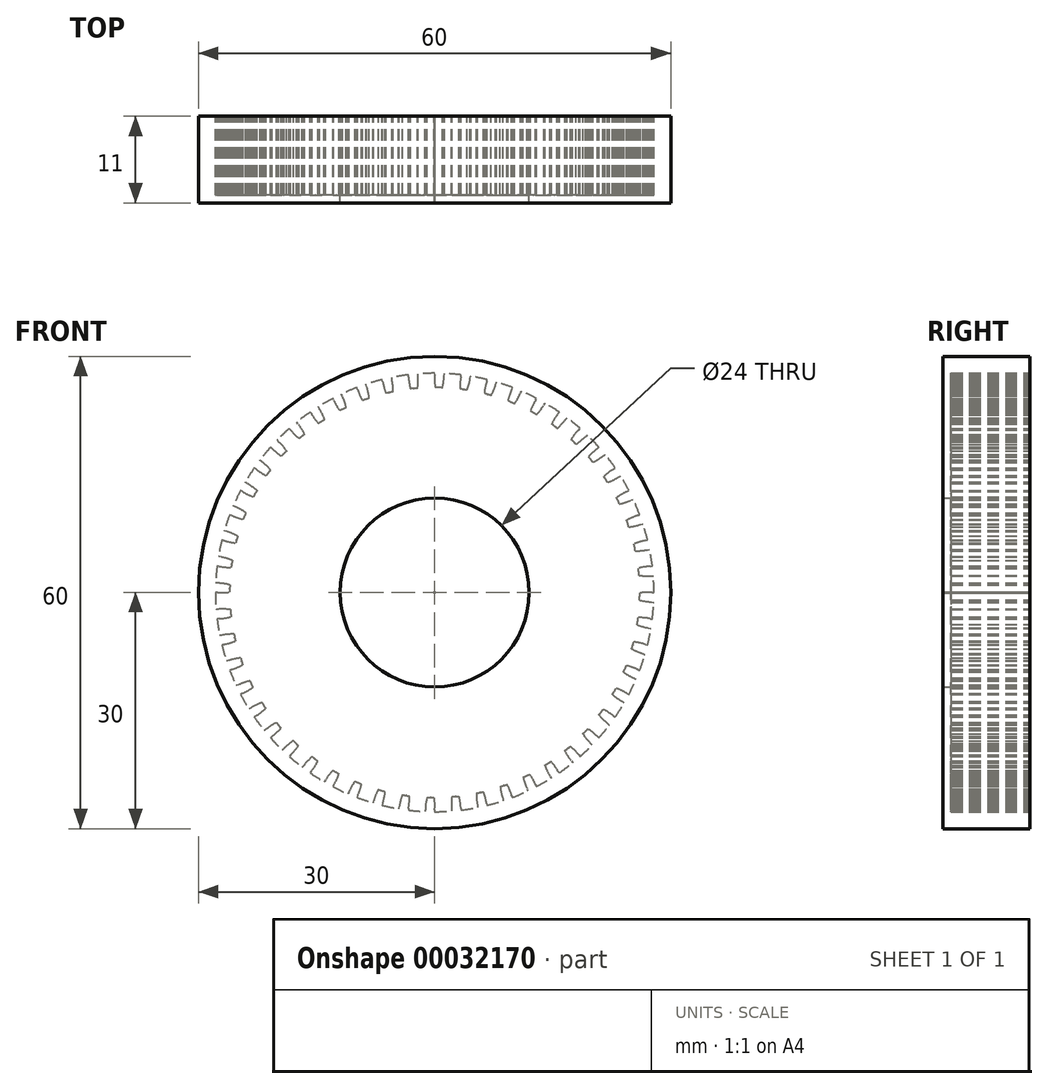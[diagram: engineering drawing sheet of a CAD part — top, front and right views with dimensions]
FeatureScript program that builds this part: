
annotation { "Feature Type Name" : "Feature", "Feature Type Description" : "" }
export const myFeature = defineFeature(function(context is Context, id is Id, definition is map)
    precondition{}
    {
        {
            var Q0;
            Q0=qCreatedBy(makeId("Front.planeOp"),FACE);
            var sketch = newSketch(context, id + "F0", { "sketchPlane" : qUnion([Q0])});
            skArc(sketch, "E0", {"start": v(-0.76, 9.47) * mm, "mid": v(-0.88, 9.46) * mm, "end": v(-1, 9.45) * mm});
            skArc(sketch, "E1", {"start": v(-1.33, 7.13) * mm, "mid": v(-1.98, 6.97) * mm, "end": v(-2.62, 6.76) * mm});
            skLineSegment(sketch, "E2", {"start": v(0, 7.25) * mm, "end": v(0, 8.5) * mm});
            skArc(sketch, "E3", {"start": v(0, 8.5) * mm, "mid": v(-0.3, 9.04) * mm, "end": v(-0.76, 9.47) * mm});
            skArc(sketch, "E4.0.MirrorCS", {"start": v(-1.56, 8.36) * mm, "mid": v(-1.36, 8.94) * mm, "end": v(-1, 9.45) * mm});
            skLineSegment(sketch, "E5.0.MirrorCS", {"start": v(-1.33, 7.13) * mm, "end": v(-1.56, 8.36) * mm});
            skLineSegment(sketch, "E6.1.0", {"start": v(-2.62, 6.76) * mm, "end": v(-3.07, 7.93) * mm});
            skArc(sketch, "E6.1.1", {"start": v(-4.47, 7.23) * mm, "mid": v(-4.5, 7.85) * mm, "end": v(-4.34, 8.45) * mm});
            skArc(sketch, "E6.1.2", {"start": v(-3.07, 7.93) * mm, "mid": v(-3.55, 8.32) * mm, "end": v(-4.13, 8.56) * mm});
            skLineSegment(sketch, "E6.1.3", {"start": v(-3.82, 6.16) * mm, "end": v(-4.47, 7.23) * mm});
            skArc(sketch, "E6.1.4", {"start": v(-4.13, 8.56) * mm, "mid": v(-4.23, 8.5) * mm, "end": v(-4.34, 8.45) * mm});
            skLineSegment(sketch, "E6.2.0", {"start": v(-4.88, 5.36) * mm, "end": v(-5.73, 6.28) * mm});
            skArc(sketch, "E6.2.1", {"start": v(-6.78, 5.12) * mm, "mid": v(-7.03, 5.7) * mm, "end": v(-7.1, 6.31) * mm});
            skArc(sketch, "E6.2.2", {"start": v(-5.73, 6.28) * mm, "mid": v(-6.32, 6.48) * mm, "end": v(-6.94, 6.49) * mm});
            skLineSegment(sketch, "E6.2.3", {"start": v(-5.78, 4.37) * mm, "end": v(-6.78, 5.12) * mm});
            skArc(sketch, "E6.2.4", {"start": v(-6.94, 6.49) * mm, "mid": v(-7.02, 6.4) * mm, "end": v(-7.1, 6.31) * mm});
            skLineSegment(sketch, "E6.3.0", {"start": v(-6.49, 3.23) * mm, "end": v(-7.6, 3.79) * mm});
            skArc(sketch, "E6.3.1", {"start": v(-8.18, 2.33) * mm, "mid": v(-8.61, 2.77) * mm, "end": v(-8.9, 3.32) * mm});
            skArc(sketch, "E6.3.2", {"start": v(-7.6, 3.79) * mm, "mid": v(-8.23, 3.76) * mm, "end": v(-8.81, 3.54) * mm});
            skLineSegment(sketch, "E6.3.3", {"start": v(-6.97, 1.99) * mm, "end": v(-8.18, 2.33) * mm});
            skArc(sketch, "E6.3.4", {"start": v(-8.81, 3.54) * mm, "mid": v(-8.86, 3.43) * mm, "end": v(-8.9, 3.32) * mm});
            skLineSegment(sketch, "E6.4.0", {"start": v(-7.22, 0.67) * mm, "end": v(-8.46, 0.78) * mm});
            skArc(sketch, "E6.4.1", {"start": v(-8.46, -0.78) * mm, "mid": v(-9.03, -0.53) * mm, "end": v(-9.5, -0.12) * mm});
            skArc(sketch, "E6.4.2", {"start": v(-8.46, 0.78) * mm, "mid": v(-9.03, 0.53) * mm, "end": v(-9.5, 0.12) * mm});
            skLineSegment(sketch, "E6.4.3", {"start": v(-7.22, -0.67) * mm, "end": v(-8.46, -0.78) * mm});
            skArc(sketch, "E6.4.4", {"start": v(-9.5, 0.12) * mm, "mid": v(-9.5, 0) * mm, "end": v(-9.5, -0.12) * mm});
            skLineSegment(sketch, "E6.5.0", {"start": v(-6.97, -1.98) * mm, "end": v(-8.18, -2.33) * mm});
            skArc(sketch, "E6.5.1", {"start": v(-7.6, -3.79) * mm, "mid": v(-8.23, -3.75) * mm, "end": v(-8.81, -3.54) * mm});
            skArc(sketch, "E6.5.2", {"start": v(-8.18, -2.33) * mm, "mid": v(-8.61, -2.77) * mm, "end": v(-8.9, -3.32) * mm});
            skLineSegment(sketch, "E6.5.3", {"start": v(-6.5, -3.23) * mm, "end": v(-7.6, -3.79) * mm});
            skArc(sketch, "E6.5.4", {"start": v(-8.9, -3.32) * mm, "mid": v(-8.86, -3.43) * mm, "end": v(-8.81, -3.54) * mm});
            skLineSegment(sketch, "E6.6.0", {"start": v(-5.79, -4.37) * mm, "end": v(-6.78, -5.12) * mm});
            skArc(sketch, "E6.6.1", {"start": v(-5.73, -6.28) * mm, "mid": v(-6.32, -6.47) * mm, "end": v(-6.94, -6.49) * mm});
            skArc(sketch, "E6.6.2", {"start": v(-6.78, -5.12) * mm, "mid": v(-7.03, -5.7) * mm, "end": v(-7.1, -6.3) * mm});
            skLineSegment(sketch, "E6.6.3", {"start": v(-4.89, -5.36) * mm, "end": v(-5.73, -6.28) * mm});
            skArc(sketch, "E6.6.4", {"start": v(-7.1, -6.3) * mm, "mid": v(-7.02, -6.4) * mm, "end": v(-6.94, -6.49) * mm});
            skLineSegment(sketch, "E6.7.0", {"start": v(-3.82, -6.16) * mm, "end": v(-4.47, -7.23) * mm});
            skArc(sketch, "E6.7.1", {"start": v(-3.07, -7.93) * mm, "mid": v(-3.55, -8.32) * mm, "end": v(-4.13, -8.56) * mm});
            skArc(sketch, "E6.7.2", {"start": v(-4.47, -7.23) * mm, "mid": v(-4.5, -7.85) * mm, "end": v(-4.34, -8.45) * mm});
            skLineSegment(sketch, "E6.7.3", {"start": v(-2.62, -6.76) * mm, "end": v(-3.07, -7.93) * mm});
            skArc(sketch, "E6.7.4", {"start": v(-4.34, -8.45) * mm, "mid": v(-4.24, -8.5) * mm, "end": v(-4.13, -8.56) * mm});
            skLineSegment(sketch, "E6.8.0", {"start": v(-1.33, -7.13) * mm, "end": v(-1.56, -8.36) * mm});
            skArc(sketch, "E6.8.1", {"start": v(0, -8.5) * mm, "mid": v(-0.3, -9.04) * mm, "end": v(-0.76, -9.47) * mm});
            skArc(sketch, "E6.8.2", {"start": v(-1.56, -8.36) * mm, "mid": v(-1.36, -8.94) * mm, "end": v(-1, -9.45) * mm});
            skLineSegment(sketch, "E6.8.3", {"start": v(0, -7.25) * mm, "end": v(0, -8.5) * mm});
            skArc(sketch, "E6.8.4", {"start": v(-1, -9.45) * mm, "mid": v(-0.88, -9.46) * mm, "end": v(-0.76, -9.47) * mm});
            skLineSegment(sketch, "E6.9.0", {"start": v(1.33, -7.13) * mm, "end": v(1.56, -8.36) * mm});
            skArc(sketch, "E6.9.1", {"start": v(3.07, -7.93) * mm, "mid": v(2.98, -8.54) * mm, "end": v(2.72, -9.1) * mm});
            skArc(sketch, "E6.9.2", {"start": v(1.56, -8.36) * mm, "mid": v(1.96, -8.83) * mm, "end": v(2.48, -9.17) * mm});
            skLineSegment(sketch, "E6.9.3", {"start": v(2.62, -6.76) * mm, "end": v(3.07, -7.93) * mm});
            skArc(sketch, "E6.9.4", {"start": v(2.48, -9.17) * mm, "mid": v(2.6, -9.14) * mm, "end": v(2.72, -9.1) * mm});
            skLineSegment(sketch, "E6.10.0", {"start": v(3.82, -6.16) * mm, "end": v(4.47, -7.23) * mm});
            skArc(sketch, "E6.10.1", {"start": v(5.73, -6.28) * mm, "mid": v(5.86, -6.89) * mm, "end": v(5.82, -7.5) * mm});
            skArc(sketch, "E6.10.2", {"start": v(4.47, -7.23) * mm, "mid": v(5.02, -7.53) * mm, "end": v(5.63, -7.65) * mm});
            skLineSegment(sketch, "E6.10.3", {"start": v(4.88, -5.36) * mm, "end": v(5.73, -6.28) * mm});
            skArc(sketch, "E6.10.4", {"start": v(5.63, -7.65) * mm, "mid": v(5.72, -7.58) * mm, "end": v(5.82, -7.5) * mm});
            skLineSegment(sketch, "E6.11.0", {"start": v(5.79, -4.37) * mm, "end": v(6.78, -5.12) * mm});
            skArc(sketch, "E6.11.1", {"start": v(7.6, -3.79) * mm, "mid": v(7.96, -4.3) * mm, "end": v(8.14, -4.9) * mm});
            skArc(sketch, "E6.11.2", {"start": v(6.78, -5.12) * mm, "mid": v(7.4, -5.2) * mm, "end": v(8.01, -5.1) * mm});
            skLineSegment(sketch, "E6.11.3", {"start": v(6.49, -3.23) * mm, "end": v(7.6, -3.79) * mm});
            skArc(sketch, "E6.11.4", {"start": v(8.01, -5.1) * mm, "mid": v(8.08, -5) * mm, "end": v(8.14, -4.9) * mm});
            skLineSegment(sketch, "E6.12.0", {"start": v(6.97, -1.98) * mm, "end": v(8.18, -2.33) * mm});
            skArc(sketch, "E6.12.1", {"start": v(8.46, -0.79) * mm, "mid": v(8.97, -1.14) * mm, "end": v(9.36, -1.63) * mm});
            skArc(sketch, "E6.12.2", {"start": v(8.18, -2.33) * mm, "mid": v(8.78, -2.18) * mm, "end": v(9.32, -1.86) * mm});
            skLineSegment(sketch, "E6.12.3", {"start": v(7.22, -0.67) * mm, "end": v(8.46, -0.79) * mm});
            skArc(sketch, "E6.12.4", {"start": v(9.32, -1.86) * mm, "mid": v(9.34, -1.75) * mm, "end": v(9.36, -1.63) * mm});
            skLineSegment(sketch, "E6.13.0", {"start": v(7.22, 0.67) * mm, "end": v(8.46, 0.78) * mm});
            skArc(sketch, "E6.13.1", {"start": v(8.18, 2.32) * mm, "mid": v(8.78, 2.18) * mm, "end": v(9.32, 1.86) * mm});
            skArc(sketch, "E6.13.2", {"start": v(8.46, 0.78) * mm, "mid": v(8.97, 1.14) * mm, "end": v(9.36, 1.63) * mm});
            skLineSegment(sketch, "E6.13.3", {"start": v(6.97, 1.98) * mm, "end": v(8.18, 2.32) * mm});
            skArc(sketch, "E6.13.4", {"start": v(9.36, 1.63) * mm, "mid": v(9.34, 1.74) * mm, "end": v(9.32, 1.86) * mm});
            skLineSegment(sketch, "E6.14.0", {"start": v(6.49, 3.23) * mm, "end": v(7.6, 3.79) * mm});
            skArc(sketch, "E6.14.1", {"start": v(6.78, 5.12) * mm, "mid": v(7.4, 5.2) * mm, "end": v(8.01, 5.1) * mm});
            skArc(sketch, "E6.14.2", {"start": v(7.6, 3.79) * mm, "mid": v(7.96, 4.3) * mm, "end": v(8.14, 4.9) * mm});
            skLineSegment(sketch, "E6.14.3", {"start": v(5.79, 4.37) * mm, "end": v(6.78, 5.12) * mm});
            skArc(sketch, "E6.14.4", {"start": v(8.14, 4.9) * mm, "mid": v(8.08, 5) * mm, "end": v(8.01, 5.1) * mm});
            skLineSegment(sketch, "E6.15.0", {"start": v(4.88, 5.36) * mm, "end": v(5.73, 6.28) * mm});
            skArc(sketch, "E6.15.1", {"start": v(4.48, 7.23) * mm, "mid": v(5.02, 7.52) * mm, "end": v(5.63, 7.65) * mm});
            skArc(sketch, "E6.15.2", {"start": v(5.73, 6.28) * mm, "mid": v(5.86, 6.89) * mm, "end": v(5.82, 7.5) * mm});
            skLineSegment(sketch, "E6.15.3", {"start": v(3.82, 6.16) * mm, "end": v(4.48, 7.23) * mm});
            skArc(sketch, "E6.15.4", {"start": v(5.82, 7.5) * mm, "mid": v(5.73, 7.58) * mm, "end": v(5.63, 7.65) * mm});
            skLineSegment(sketch, "E6.16.0", {"start": v(2.62, 6.76) * mm, "end": v(3.07, 7.93) * mm});
            skArc(sketch, "E6.16.1", {"start": v(1.56, 8.36) * mm, "mid": v(1.96, 8.83) * mm, "end": v(2.48, 9.17) * mm});
            skArc(sketch, "E6.16.2", {"start": v(3.07, 7.93) * mm, "mid": v(2.98, 8.54) * mm, "end": v(2.72, 9.1) * mm});
            skLineSegment(sketch, "E6.16.3", {"start": v(1.33, 7.13) * mm, "end": v(1.56, 8.36) * mm});
            skArc(sketch, "E6.16.4", {"start": v(2.72, 9.1) * mm, "mid": v(2.6, 9.14) * mm, "end": v(2.48, 9.17) * mm});
            skArc(sketch, "E7.trimOffspring", {"start": v(1.33, 7.13) * mm, "mid": v(0.67, 7.22) * mm, "end": v(0, 7.25) * mm});
            skArc(sketch, "E8.trimOffspring", {"start": v(3.82, 6.16) * mm, "mid": v(3.23, 6.49) * mm, "end": v(2.62, 6.76) * mm});
            skArc(sketch, "E9.trimOffspring", {"start": v(5.79, 4.37) * mm, "mid": v(5.36, 4.88) * mm, "end": v(4.88, 5.36) * mm});
            skArc(sketch, "E10.trimOffspring", {"start": v(6.97, 1.98) * mm, "mid": v(6.76, 2.62) * mm, "end": v(6.49, 3.23) * mm});
            skArc(sketch, "E11.trimOffspring", {"start": v(7.22, -0.67) * mm, "mid": v(7.25, 0) * mm, "end": v(7.22, 0.67) * mm});
            skArc(sketch, "E12.trimOffspring", {"start": v(6.49, -3.23) * mm, "mid": v(6.76, -2.62) * mm, "end": v(6.97, -1.98) * mm});
            skArc(sketch, "E13.trimOffspring", {"start": v(4.88, -5.36) * mm, "mid": v(5.36, -4.88) * mm, "end": v(5.79, -4.37) * mm});
            skArc(sketch, "E14.trimOffspring", {"start": v(2.62, -6.76) * mm, "mid": v(3.23, -6.5) * mm, "end": v(3.82, -6.16) * mm});
            skArc(sketch, "E15.trimOffspring", {"start": v(0, -7.25) * mm, "mid": v(0.67, -7.22) * mm, "end": v(1.33, -7.13) * mm});
            skArc(sketch, "E16.trimOffspring", {"start": v(-2.62, -6.76) * mm, "mid": v(-1.98, -6.97) * mm, "end": v(-1.33, -7.13) * mm});
            skArc(sketch, "E17.trimOffspring", {"start": v(-4.89, -5.36) * mm, "mid": v(-4.37, -5.79) * mm, "end": v(-3.82, -6.16) * mm});
            skArc(sketch, "E18.trimOffspring", {"start": v(-6.5, -3.23) * mm, "mid": v(-6.16, -3.82) * mm, "end": v(-5.79, -4.37) * mm});
            skArc(sketch, "E19.trimOffspring", {"start": v(-7.22, -0.67) * mm, "mid": v(-7.13, -1.33) * mm, "end": v(-6.97, -1.98) * mm});
            skArc(sketch, "E20.trimOffspring", {"start": v(-6.97, 1.99) * mm, "mid": v(-7.13, 1.33) * mm, "end": v(-7.22, 0.67) * mm});
            skArc(sketch, "E21.trimOffspring", {"start": v(-5.78, 4.37) * mm, "mid": v(-6.16, 3.82) * mm, "end": v(-6.49, 3.23) * mm});
            skArc(sketch, "E22.trimOffspring", {"start": v(-3.82, 6.16) * mm, "mid": v(-4.37, 5.79) * mm, "end": v(-4.88, 5.36) * mm});
            skCircle(sketch, "E23", {"center": v(0, 0) * mm, "radius": 4 * mm});
            skLineSegment(sketch, "E24", {"start": v(-0.42, 17.6) * mm, "end": v(1.16, 17.6) * mm, "construction": true});
            skLineSegment(sketch, "E25", {"start": v(0, 18.2) * mm, "end": v(0, 16.94) * mm, "construction": true});
            skArc(sketch, "E26", {"start": v(-3.08, 26.06) * mm, "mid": v(-1.05, 8.66) * mm, "end": v(4.95, 25.12) * mm});
            skArc(sketch, "E27", {"start": v(-0.73, 27.57) * mm, "mid": v(-0.8, 27.57) * mm, "end": v(-0.87, 27.56) * mm});
            skArc(sketch, "E28", {"start": v(-0.79, 26.59) * mm, "mid": v(0.12, -26.6) * mm, "end": v(0.54, 26.6) * mm});
            skCircle(sketch, "E29", {"center": v(0, 17.6) * mm, "radius": 7.75 * mm});
            skCircle(sketch, "E30", {"center": v(0, 0) * mm, "radius": 27.85 * mm});
            skCircle(sketch, "E31", {"center": v(0, 0) * mm, "radius": 25.6 * mm});
            skArc(sketch, "E32", {"start": v(-1.47, 25.93) * mm, "mid": v(-2.4, 25.7) * mm, "end": v(-3.3, 25.39) * mm});
            skLineSegment(sketch, "E33", {"start": v(0, 17.6) * mm, "end": v(0, 26.6) * mm, "construction": true});
            skLineSegment(sketch, "E34", {"start": v(0, 17.6) * mm, "end": v(-0.98, 28.75) * mm, "construction": true});
            skCircle(sketch, "E35", {"center": v(0, 17.6) * mm, "radius": 8 * mm, "construction": true});
            skLineSegment(sketch, "E36", {"start": v(0, 26.6) * mm, "end": v(0, 26.06) * mm});
            skLineSegment(sketch, "E37.trimOffspring", {"start": v(0, 25.6) * mm, "end": v(0, 25.6) * mm});
            skArc(sketch, "E38.trimOffspring", {"start": v(-5.33, 26.06) * mm, "mid": v(2.49, 7.91) * mm, "end": v(0.6, 27.58) * mm});
            skArc(sketch, "E39.0.MirrorCS", {"start": v(-1.02, 27.55) * mm, "mid": v(-0.94, 27.56) * mm, "end": v(-0.87, 27.56) * mm});
            skArc(sketch, "E40.0.MirrorCS", {"start": v(-1.56, 26.46) * mm, "mid": v(-1.36, 27.04) * mm, "end": v(-1.02, 27.55) * mm});
            skLineSegment(sketch, "E41.0.MirrorCS", {"start": v(-1.56, 26.46) * mm, "end": v(-1.47, 25.93) * mm});
            skLineSegment(sketch, "E42", {"start": v(0, 17.6) * mm, "end": v(-4, 28.58) * mm, "construction": true});
            skArc(sketch, "E43.trimOffspring", {"start": v(-1.18, 9.23) * mm, "mid": v(8.41, 16.75) * mm, "end": v(0.51, 26.04) * mm});
            skLineSegment(sketch, "E44", {"start": v(0, 17.6) * mm, "end": v(0.98, 17.69) * mm, "construction": true});
            skArc(sketch, "E45.0.MirrorCS", {"start": v(0, 8.6) * mm, "mid": v(0.3, 8.06) * mm, "end": v(0.73, 7.63) * mm});
            skLineSegment(sketch, "E46.0.MirrorCS", {"start": v(0, 8.6) * mm, "end": v(0, 9.14) * mm});
            skArc(sketch, "E47.0.MirrorCS", {"start": v(1.56, 8.74) * mm, "mid": v(1.36, 8.16) * mm, "end": v(1.02, 7.65) * mm});
            skLineSegment(sketch, "E48.0.MirrorCS", {"start": v(1.56, 8.74) * mm, "end": v(1.47, 9.27) * mm});
            skArc(sketch, "E49.0.MirrorCS", {"start": v(1.02, 7.65) * mm, "mid": v(0.94, 7.64) * mm, "end": v(0.87, 7.64) * mm});
            skArc(sketch, "E49.1.MirrorCS", {"start": v(0.73, 7.63) * mm, "mid": v(0.8, 7.63) * mm, "end": v(0.87, 7.64) * mm});
            skLineSegment(sketch, "E50", {"start": v(0, 0) * mm, "end": v(0, -29.5) * mm, "construction": true});
            skLineSegment(sketch, "E51", {"start": v(0, 0) * mm, "end": v(1.8, -29.89) * mm, "construction": true});
            skLineSegment(sketch, "E52", {"start": v(0, 0) * mm, "end": v(0.96, -31.81) * mm, "construction": true});
            skLineSegment(sketch, "E53", {"start": v(0, 17.6) * mm, "end": v(1.5, 29.97) * mm, "construction": true});
            skLineSegment(sketch, "E54", {"start": v(0, 17.6) * mm, "end": v(0.42, 31.47) * mm, "construction": true});
            skCircle(sketch, "E55", {"center": v(0, 0) * mm, "radius": 25 * mm, "construction": true});
            skArc(sketch, "E56.trimOffspring", {"start": v(0, 27.6) * mm, "mid": v(-0.01, 26.83) * mm, "end": v(0.06, 26.05) * mm});
            skArc(sketch, "E57.trimOffspring", {"start": v(0.26, 26.05) * mm, "mid": v(0.16, 26.05) * mm, "end": v(0.06, 26.05) * mm});
            skLineSegment(sketch, "E58.0.MirrorCS", {"start": v(0.54, 26.58) * mm, "end": v(0.66, 28.55) * mm, "construction": true});
            skArc(sketch, "E59.0.MirrorCS", {"start": v(0.26, 26.05) * mm, "mid": v(0.35, 26.05) * mm, "end": v(0.45, 26.04) * mm});
            skCircle(sketch, "E60", {"center": v(0, 0) * mm, "radius": 30 * mm});
            skCircle(sketch, "E61", {"center": v(0, 0) * mm, "radius": 0.05 * mm});
            skArc(sketch, "E62.trimOffspring", {"start": v(0.54, 26.6) * mm, "mid": v(0.54, 26.59) * mm, "end": v(0.54, 26.58) * mm});
            skArc(sketch, "E63.0.MirrorCS", {"start": v(1.2, 27.53) * mm, "mid": v(1.12, 26.76) * mm, "end": v(0.96, 26) * mm});
            skArc(sketch, "E64.0.MirrorCS", {"start": v(0.76, 26.02) * mm, "mid": v(0.86, 26.01) * mm, "end": v(0.96, 26) * mm});
            skArc(sketch, "E65.0.MirrorCS", {"start": v(0.76, 26.02) * mm, "mid": v(0.67, 26.03) * mm, "end": v(0.57, 26.04) * mm});
            skLineSegment(sketch, "E66.0.MirrorCS", {"start": v(1.2, 27.53) * mm, "end": v(1.23, 27.78) * mm});
            skLineSegment(sketch, "E67", {"start": v(0.45, 26.04) * mm, "end": v(0.51, 26.04) * mm});
            skPoint(sketch, "E68.end.orphan", {"position": v(0, 27.85) * mm});
            skLineSegment(sketch, "E69", {"start": v(0, 27.6) * mm, "end": v(0, 27.85) * mm});
            skLineSegment(sketch, "E70", {"start": v(1.23, 27.78) * mm, "end": v(1.24, 27.82) * mm});
            skSolve(sketch);
        }
        {
            var Q0;
            Q0=makeQuery(id+"F0.imprint","IMPRINT",FACE,{"disambiguationData":[TD([[makeQuery(id+"F0.imprint","IMPRINT",EDGE,{"derivedFrom":sQuery(id+"F0.wireOp",EDGE,"E60")}),1.0]])]});
            var Q1;
            {var subQ7=sQuery(id+"F0.wireOp",EDGE,"E57.trimOffspring");Q1=makeQuery(id+"F0.imprint","IMPRINT",FACE,{"disambiguationData":[TD([[makeQuery(id+"F0.imprint","IMPRINT",EDGE,{"derivedFrom":subQ7}),-1.0]])]});}
            var Q2;
            Q2=makeQuery(id+"F0.imprint","IMPRINT",FACE,{"disambiguationData":[TD([[makeQuery(id+"F0.imprint","IMPRINT",EDGE,{"derivedFrom":sQuery(id+"F0.wireOp",EDGE,"E61")}),1.0]])]});
            extrude(context, id + "F1", {"entities" : qUnion([Q0, Q1, Q2]), "depth" : 10 * mm});
        }
        {
            var Q0;
            Q0=makeQuery(id+"F1.opExtrude","SWEPT_BODY",BODY,{"disambiguationData":[OSD([sQuery(id+"F0.wireOp",EDGE,"E30"),sQuery(id+"F0.wireOp",EDGE,"E43.trimOffspring"),sQuery(id+"F0.wireOp",EDGE,"E56.trimOffspring"),sQuery(id+"F0.wireOp",EDGE,"E57.trimOffspring"),sQuery(id+"F0.wireOp",EDGE,"E59.0.MirrorCS"),sQuery(id+"F0.wireOp",EDGE,"E60"),sQuery(id+"F0.wireOp",EDGE,"E63.0.MirrorCS"),sQuery(id+"F0.wireOp",EDGE,"E64.0.MirrorCS"),sQuery(id+"F0.wireOp",EDGE,"E65.0.MirrorCS"),sQuery(id+"F0.wireOp",EDGE,"E66.0.MirrorCS"),sQuery(id+"F0.wireOp",EDGE,"E67"),sQuery(id+"F0.wireOp",EDGE,"E69"),sQuery(id+"F0.wireOp",EDGE,"E70")])]});
            var Q1;
            Q1=makeQuery(id+"F1.opExtrude","SWEPT_FACE",FACE,{"disambiguationData":[OSD([sQuery(id+"F0.wireOp",EDGE,"E61")])]});
            circularPattern(context, id + "F2", {"entities" : qUnion([Q0]), "axis" : qUnion([Q1]), "angle" : 6.92 * degree, "instanceCount" : round(52)});
        }
        {
            var Q0;
            Q0=makeQuery(id+"F2.opPattern","COPY",FACE,{"derivedFrom":makeQuery(id+"F1.opExtrude","CAP_FACE",FACE,{"disambiguationData":[OSD([sQuery(id+"F0.wireOp",EDGE,"E30"),sQuery(id+"F0.wireOp",EDGE,"E43.trimOffspring"),sQuery(id+"F0.wireOp",EDGE,"E56.trimOffspring"),sQuery(id+"F0.wireOp",EDGE,"E57.trimOffspring"),sQuery(id+"F0.wireOp",EDGE,"E59.0.MirrorCS"),sQuery(id+"F0.wireOp",EDGE,"E60"),sQuery(id+"F0.wireOp",EDGE,"E63.0.MirrorCS"),sQuery(id+"F0.wireOp",EDGE,"E64.0.MirrorCS"),sQuery(id+"F0.wireOp",EDGE,"E65.0.MirrorCS"),sQuery(id+"F0.wireOp",EDGE,"E66.0.MirrorCS"),sQuery(id+"F0.wireOp",EDGE,"E67"),sQuery(id+"F0.wireOp",EDGE,"E69"),sQuery(id+"F0.wireOp",EDGE,"E70")])],"isStart":false}),"instanceName":"44"});
            var sketch = newSketch(context, id + "F3", { "sketchPlane" : qUnion([Q0])});
            skCircle(sketch, "E71.0", {"center": v(0, 0) * mm, "radius": 30 * mm});
            skSolve(sketch);
        }
        {
            var Q0;
            {var subQ8=makeQuery(id+"F3.imprint","IMPRINT",EDGE,{"derivedFrom":makeQuery(id+"F2.opPattern","COPY",EDGE,{"derivedFrom":makeQuery(id+"F1.opExtrude","CAP_EDGE",EDGE,{"disambiguationData":[OSD([sQuery(id+"F0.wireOp",EDGE,"E30")])],"isStart":false}),"instanceName":"44"})});Q0=qUnion([makeQuery(id+"F3.imprint","IMPRINT",FACE,{"disambiguationData":[TD([[makeQuery(id+"F3.imprint","IMPRINT",EDGE,{"derivedFrom":sQuery(id+"F3.wireOp",EDGE,"E71.0")}),1.0]])]}),makeQuery(id+"F3.imprint","IMPRINT",FACE,{"disambiguationData":[TD([[subQ8,1.0]])]})]);}
            extrude(context, id + "F4", {"entities" : qUnion([Q0]), "operationType" : NewBodyOperationType.ADD, "depth" : 1 * mm});
        }
        {
            var Q0;
            Q0=makeQuery(id+"F4.opExtrude","CAP_FACE",FACE,{"disambiguationData":[OSD([sQuery(id+"F3.wireOp",EDGE,"E71.0")])],"isStart":true});
            var sketch = newSketch(context, id + "F5", { "sketchPlane" : qUnion([Q0])});
            skCircle(sketch, "E72", {"center": v(0, 0) * mm, "radius": 12 * mm});
            skSolve(sketch);
        }
        {
            var Q0;
            Q0=makeQuery(id+"F5.imprint","IMPRINT",FACE,{"disambiguationData":[TD([[makeQuery(id+"F5.imprint","IMPRINT",EDGE,{"derivedFrom":sQuery(id+"F5.wireOp",EDGE,"E72")}),1.0]])]});
            extrude(context, id + "F6", {"entities" : qUnion([Q0]), "operationType" : NewBodyOperationType.REMOVE, "endBound" : BoundingType.UP_TO_NEXT, "oppositeDirection" : true, "depth" : 25 * mm});
        }
    });
